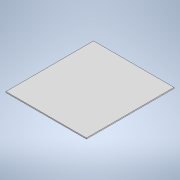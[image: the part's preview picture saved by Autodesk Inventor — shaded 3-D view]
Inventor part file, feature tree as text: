
AUTODESK INVENTOR PART (.ipt)
format: ipt  version: 2022 (Build 260153000, 153)  size: 89,600 bytes
history: native  units: mm
features: extrude x1, sketch x1
ambient origin geometry x8: Origin, YZ Plane, XZ Plane, XY Plane, X Axis, Y Axis, Z Axis, Center Point
bodies: Solid1 (feature_tree)
feature tree (2):
  extrude  "Extrusion1"  Depth=110.5mm
  sketch  "Sketch1"  dims[d0=101.5mm d1=110.5mm d2=1.25mm d3=0.0mm]
